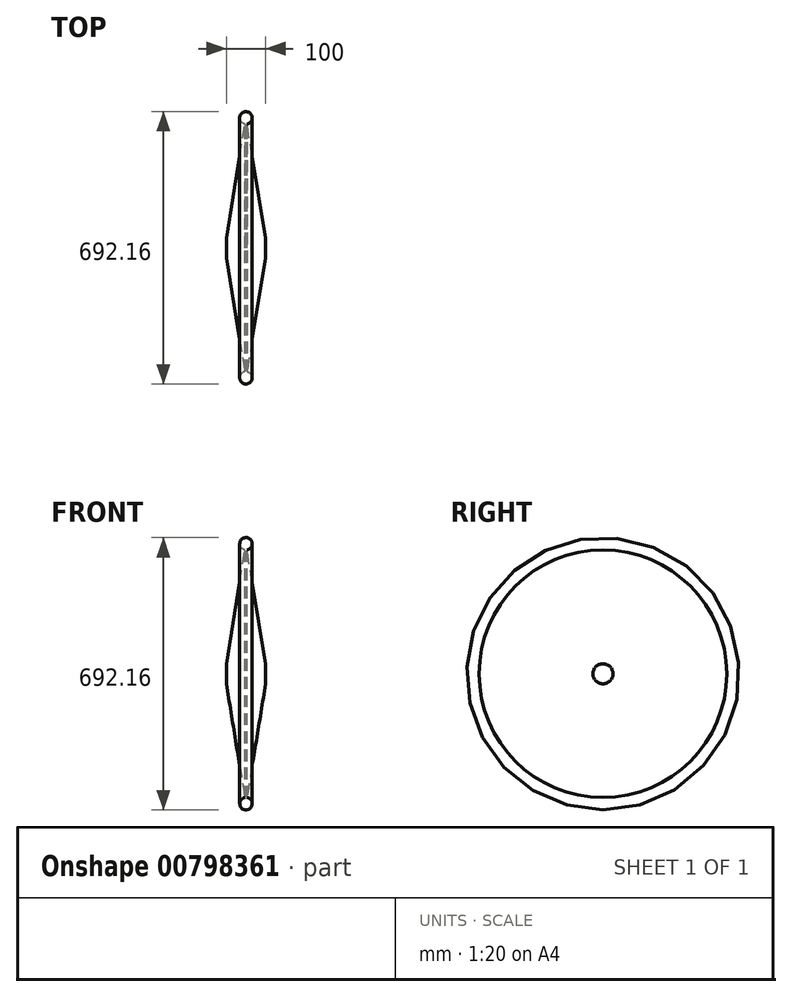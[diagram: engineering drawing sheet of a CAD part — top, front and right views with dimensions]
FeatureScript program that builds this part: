
annotation { "Feature Type Name" : "Feature", "Feature Type Description" : "" }
export const myFeature = defineFeature(function(context is Context, id is Id, definition is map)
    precondition{}
    {
        {
            var Q0;
            Q0=qCreatedBy(makeId("Front.planeOp"),FACE);
            var sketch = newSketch(context, id + "F0", { "sketchPlane" : qUnion([Q0])});
            skLineSegment(sketch, "E0", {"start": v(50, 0) * mm, "end": v(-50, 0) * mm});
            skLineSegment(sketch, "E1", {"start": v(-50, 0) * mm, "end": v(-50, 25.4) * mm});
            skLineSegment(sketch, "E2", {"start": v(50, 0) * mm, "end": v(50, 25.4) * mm});
            skLineSegment(sketch, "E3", {"start": v(-2.57, 314.53) * mm, "end": v(-50, 25.4) * mm});
            skLineSegment(sketch, "E4", {"start": v(2.57, 314.53) * mm, "end": v(50, 25.4) * mm});
            skArc(sketch, "E5", {"start": v(2.57, 314.53) * mm, "mid": v(0, 346.08) * mm, "end": v(-2.57, 314.53) * mm});
            skSolve(sketch);
        }
        {
            var Q0;
            Q0=makeQuery(id+"F0.imprint","IMPRINT",FACE,{"disambiguationData":[TD([[makeQuery(id+"F0.imprint","IMPRINT",EDGE,{"derivedFrom":sQuery(id+"F0.wireOp",EDGE,"E0")}),-1.0]])]});
            var Q1;
            Q1=sQuery(id+"F0.wireOp",EDGE,"E0");
            revolve(context, id + "F1", {"surfaceOperationType" : NewSurfaceOperationType.NEW, "entities" : qUnion([Q0]), "axis" : qUnion([Q1]), "revolveType" : RevolveType.FULL});
        }
    });
